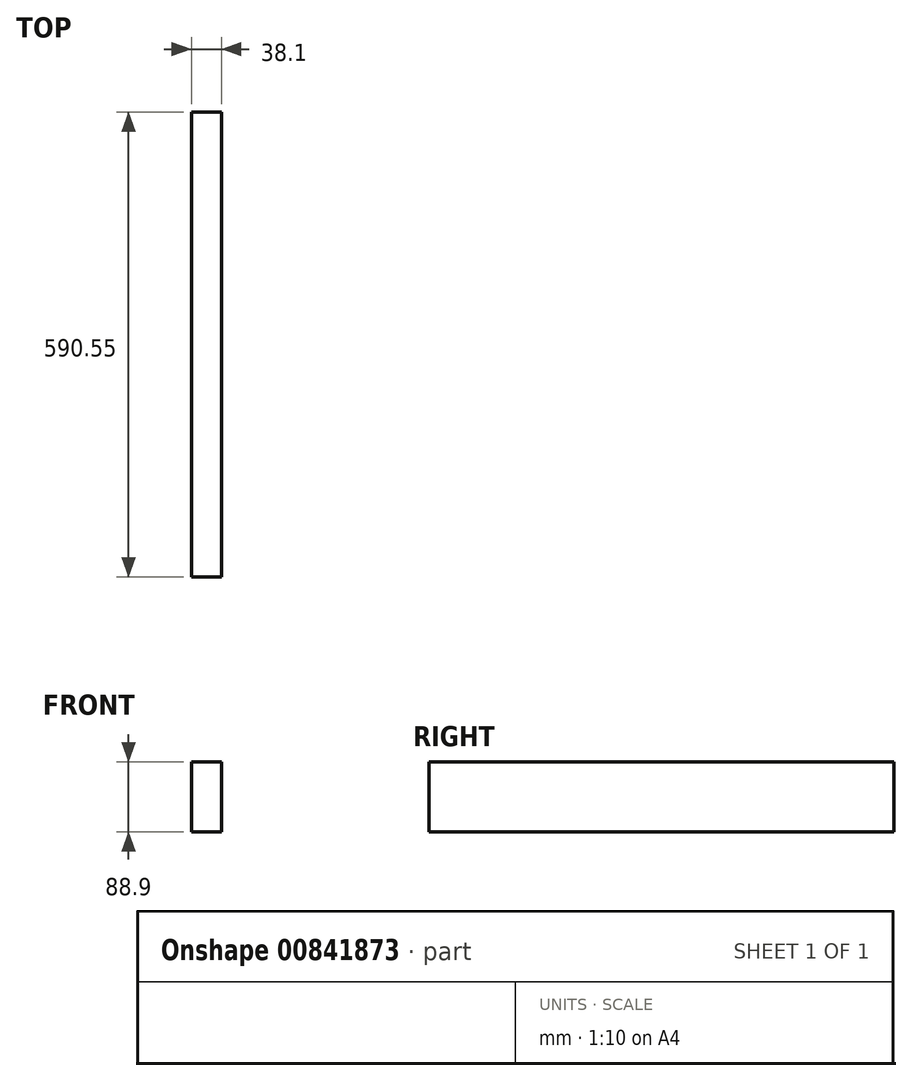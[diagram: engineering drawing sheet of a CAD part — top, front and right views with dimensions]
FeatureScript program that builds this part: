
annotation { "Feature Type Name" : "Feature", "Feature Type Description" : "" }
export const myFeature = defineFeature(function(context is Context, id is Id, definition is map)
    precondition{}
    {
        {
            var Q0;
            Q0=qCreatedBy(makeId("Front.planeOp"),FACE);
            var sketch = newSketch(context, id + "F0", { "sketchPlane" : qUnion([Q0])});
            skLineSegment(sketch, "E0.bottom", {"start": v(19.05, 44.45) * mm, "end": v(-19.05, 44.45) * mm});
            skLineSegment(sketch, "E0.top", {"start": v(19.05, -44.45) * mm, "end": v(-19.05, -44.45) * mm});
            skLineSegment(sketch, "E0.left", {"start": v(19.05, 44.45) * mm, "end": v(19.05, -44.45) * mm});
            skLineSegment(sketch, "E0.right", {"start": v(-19.05, 44.45) * mm, "end": v(-19.05, -44.45) * mm});
            skPoint(sketch, "E0.middle", {"position": v(0, 0) * mm});
            skSolve(sketch);
        }
        {
            var Q0;
            Q0 = qSketchRegion(id + "F0", true);
            extrude(context, id + "F1", {"entities" : qUnion([Q0]), "depth" : 590.55 * mm, "offsetDistance" : 25.4 * mm});
        }
    });
